# Revit family: Vertical Blinds
name_source: partatom
category: Generic Models
revit_build: Autodesk Revit Architecture 2013 (Build: 20120221_2030(x64)
units: mm (PartAtom-declared; Revit-internal decimal feet)

## types (3) — shared parameters
Default Elevation = 4' - 0"
Stripe Angle = 45.00°

## per-type parameters (varying)
| type | Rail Height | Rail Material | Rail Position | Rail Width | SLC | SLO | Stripe Depth | Stripe Material | Stripe Width | Stripes Length | Top of Stripes to Bottom of Rail | Total Blind Height | Total Rail Length |
| Type 1 | 0' - 5 9/32" | <By Category> | 0' - 2 1/8" | 0' - 2 1/16" | 17' - 10 19/32" | 17' - 10 19/32" | 0' - 0 1/2" | <By Category> | 0' - 6" | 17' - 10 19/32" | 0' - 3" | 9' - 3" | 18' - 2 27/32" |
| Type 2 | 0' - 3" | Steel, Galvanized | 0' - 1 1/16" | 0' - 2" | 8' - 1 7/8" | 4' - 0" | 0' - 0 1/8" | Fabric - Curtain | 0' - 3" | 4' - 0" | 0' - 1" | 9' - 0" | 8' - 4" |
| Type 3 | 0' - 3" | Steel, Galvanized | 0' - 1 1/16" | 0' - 2" | 10' - 8 7/8" | 4' - 0" | 0' - 0 1/8" | Fabric - Curtain | 0' - 3" | 4' - 0" | 0' - 1" | 7' - 5" | 10' - 11" |

## geometry (parser evidence)
native form markers: Sweep x2
no freeform markers — native parametric forms only
